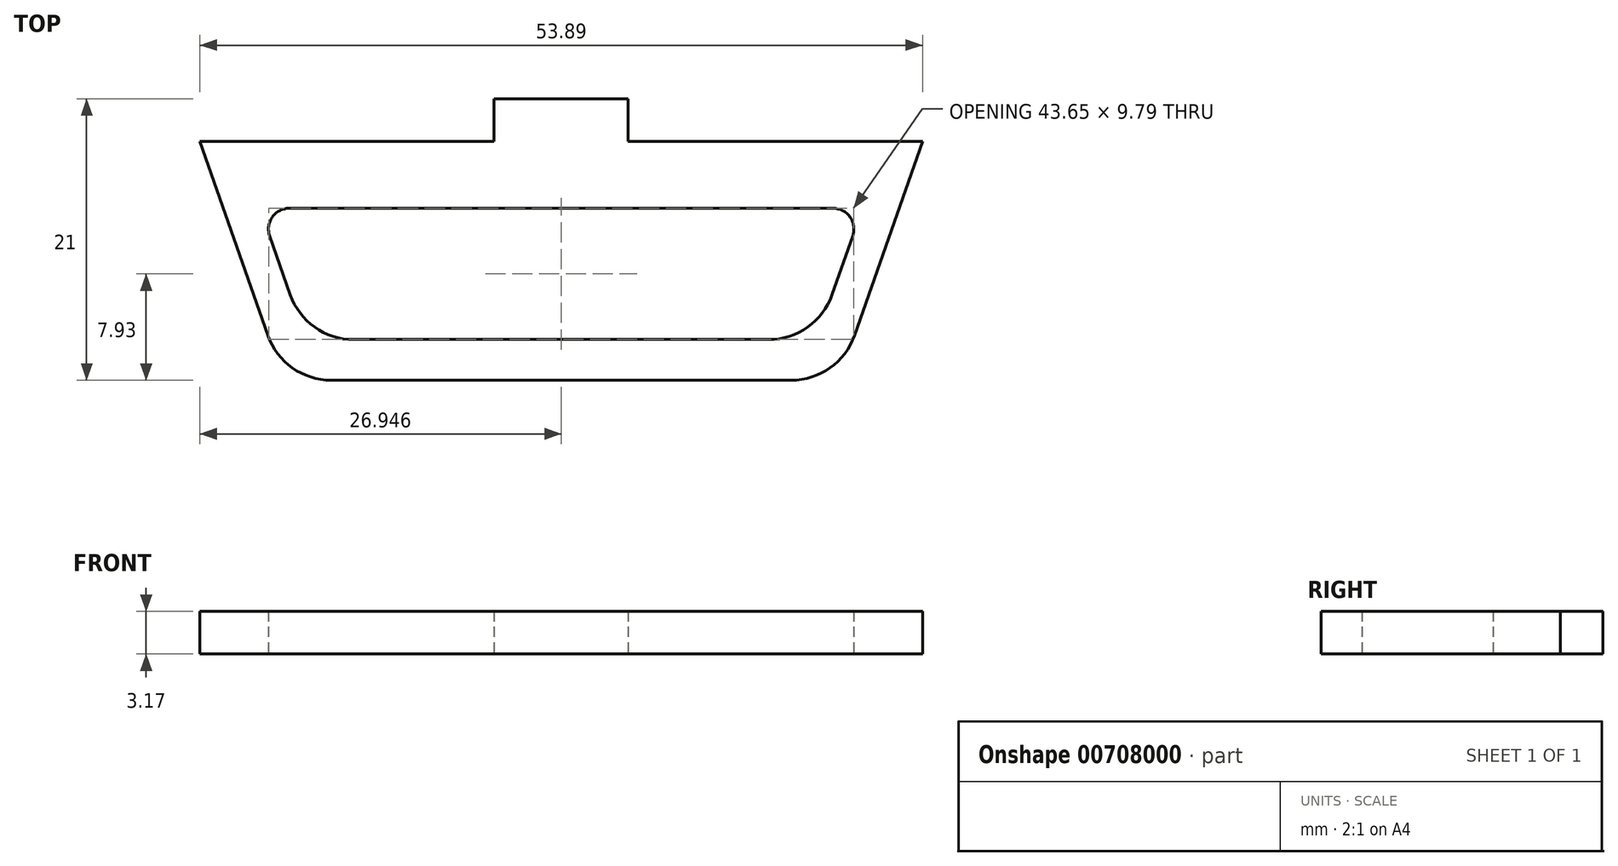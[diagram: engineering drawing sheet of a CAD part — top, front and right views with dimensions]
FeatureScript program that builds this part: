
annotation { "Feature Type Name" : "Feature", "Feature Type Description" : "" }
export const myFeature = defineFeature(function(context is Context, id is Id, definition is map)
    precondition{}
    {
        {
            var Q0;
            Q0=qCreatedBy(makeId("Top.planeOp"), FACE);
            var sketch = newSketch(context, id + "F0", { "sketchPlane" : qUnion([Q0])});
            skPoint(sketch, "E0.0", {"position": v(-28.65, 52.33) * mm});
            skPoint(sketch, "E1.0", {"position": v(25.24, 55.5) * mm});
            skPoint(sketch, "E2.0", {"position": v(25.24, 52.33) * mm});
            skPoint(sketch, "E3.0", {"position": v(31.17, 4.97) * mm});
            skPoint(sketch, "E4.0", {"position": v(-34.58, 4.97) * mm});
            skLineSegment(sketch, "E5", {"start": v(25.24, 52.33) * mm, "end": v(25.24, 4.97) * mm, "construction": true});
            skLineSegment(sketch, "E6", {"start": v(-28.65, 52.33) * mm, "end": v(-28.65, 4.97) * mm, "construction": true});
            skLineSegment(sketch, "E7.0", {"start": v(3.3, 4.97) * mm, "end": v(25.24, 4.97) * mm});
            skLineSegment(sketch, "E8.0", {"start": v(3.3, 8.15) * mm, "end": v(3.3, 4.97) * mm});
            skLineSegment(sketch, "E9.0", {"start": v(-1.7, 8.15) * mm, "end": v(3.3, 8.15) * mm});
            skPoint(sketch, "E10.0", {"position": v(-4.2, 8.15) * mm});
            skLineSegment(sketch, "E11.0", {"start": v(-1.7, 8.15) * mm, "end": v(-6.7, 8.15) * mm});
            skLineSegment(sketch, "E12.0", {"start": v(-6.7, 8.15) * mm, "end": v(-6.7, 4.97) * mm});
            skLineSegment(sketch, "E13.0", {"start": v(-28.65, 4.97) * mm, "end": v(-6.7, 4.97) * mm});
            skLineSegment(sketch, "E14", {"start": v(-28.65, 4.97) * mm, "end": v(-23.58, -9.5) * mm});
            skLineSegment(sketch, "E15", {"start": v(-18.86, -12.85) * mm, "end": v(-1.7, -12.85) * mm});
            skLineSegment(sketch, "E16.MirrorCS", {"start": v(25.24, 4.97) * mm, "end": v(20.17, -9.5) * mm});
            skLineSegment(sketch, "E17.MirrorCS", {"start": v(15.45, -12.85) * mm, "end": v(-1.7, -12.85) * mm});
            skLineSegment(sketch, "E18", {"start": v(-1.7, 8.15) * mm, "end": v(-1.7, -12.85) * mm, "construction": true});
            skPoint(sketch, "E19.visualSharp", {"position": v(19, -12.85) * mm});
            skArc(sketch, "E19.filletArc", {"start": v(15.45, -12.85) * mm, "mid": v(18.34, -11.93) * mm, "end": v(20.17, -9.5) * mm});
            skPoint(sketch, "E20.visualSharp", {"position": v(-22.4, -12.85) * mm});
            skArc(sketch, "E20.filletArc", {"start": v(-23.58, -9.5) * mm, "mid": v(-21.75, -11.93) * mm, "end": v(-18.86, -12.85) * mm});
            skPoint(sketch, "E21.0", {"position": v(19.84, -0.68) * mm});
            skLineSegment(sketch, "E22.0", {"start": v(20.04, -2.09) * mm, "end": v(18.5, -6.47) * mm});
            skArc(sketch, "E23.0", {"start": v(13.79, -9.81) * mm, "mid": v(16.68, -8.9) * mm, "end": v(18.5, -6.47) * mm});
            skArc(sketch, "E24.0", {"start": v(-21.91, -6.47) * mm, "mid": v(-20.09, -8.9) * mm, "end": v(-17.2, -9.81) * mm});
            skLineSegment(sketch, "E25.0", {"start": v(-23.45, -2.09) * mm, "end": v(-21.91, -6.47) * mm});
            skArc(sketch, "E26.0", {"start": v(-21.98, -0.03) * mm, "mid": v(-23.25, -0.68) * mm, "end": v(-23.45, -2.09) * mm});
            skArc(sketch, "E27.0", {"start": v(20.04, -2.09) * mm, "mid": v(19.84, -0.68) * mm, "end": v(18.58, -0.03) * mm});
            skLineSegment(sketch, "E28", {"start": v(18.58, -0.03) * mm, "end": v(-21.98, -0.03) * mm});
            skPoint(sketch, "E29.orphan", {"position": v(-20.53, -9.9) * mm});
            skPoint(sketch, "E30.0.end.orphan", {"position": v(17.12, -9.9) * mm});
            skLineSegment(sketch, "E31", {"start": v(13.79, -9.81) * mm, "end": v(-17.2, -9.81) * mm});
            skPoint(sketch, "E32.0.end.orphan", {"position": v(-25.46, -11.47) * mm});
            skPoint(sketch, "E32.0.start.orphan", {"position": v(-31.22, 4.97) * mm});
            skSolve(sketch);
        }
        {
            var Q0;
            Q0 = qSketchRegion(id + "F0", true);
            extrude(context, id + "F1", {"entities" : qUnion([Q0]), "depth" : 3.17 * mm, "offsetDistance" : 25 * mm});
        }
    });
